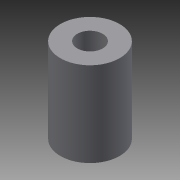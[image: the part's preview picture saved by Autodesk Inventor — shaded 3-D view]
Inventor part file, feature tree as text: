
AUTODESK INVENTOR PART (.ipt)
format: ipt  version: 2013 SP2 (Build 170200200, 200)  size: 70,144 bytes
history: native  units: mm
features: extrude x1, sketch x1
ambient origin geometry x8: Origin, YZ Plane, XZ Plane, XY Plane, X Axis, Y Axis, Z Axis, Center Point
bodies: Solid1 (feature_tree)
feature tree (2):
  extrude  "Extrusion1"  Depth=10.0mm TaperAngle=0.0deg
  sketch  "Sketch1"  dims[d0=7.0mm d1=10.0mm d2=0.0mm d3=3.0mm]
